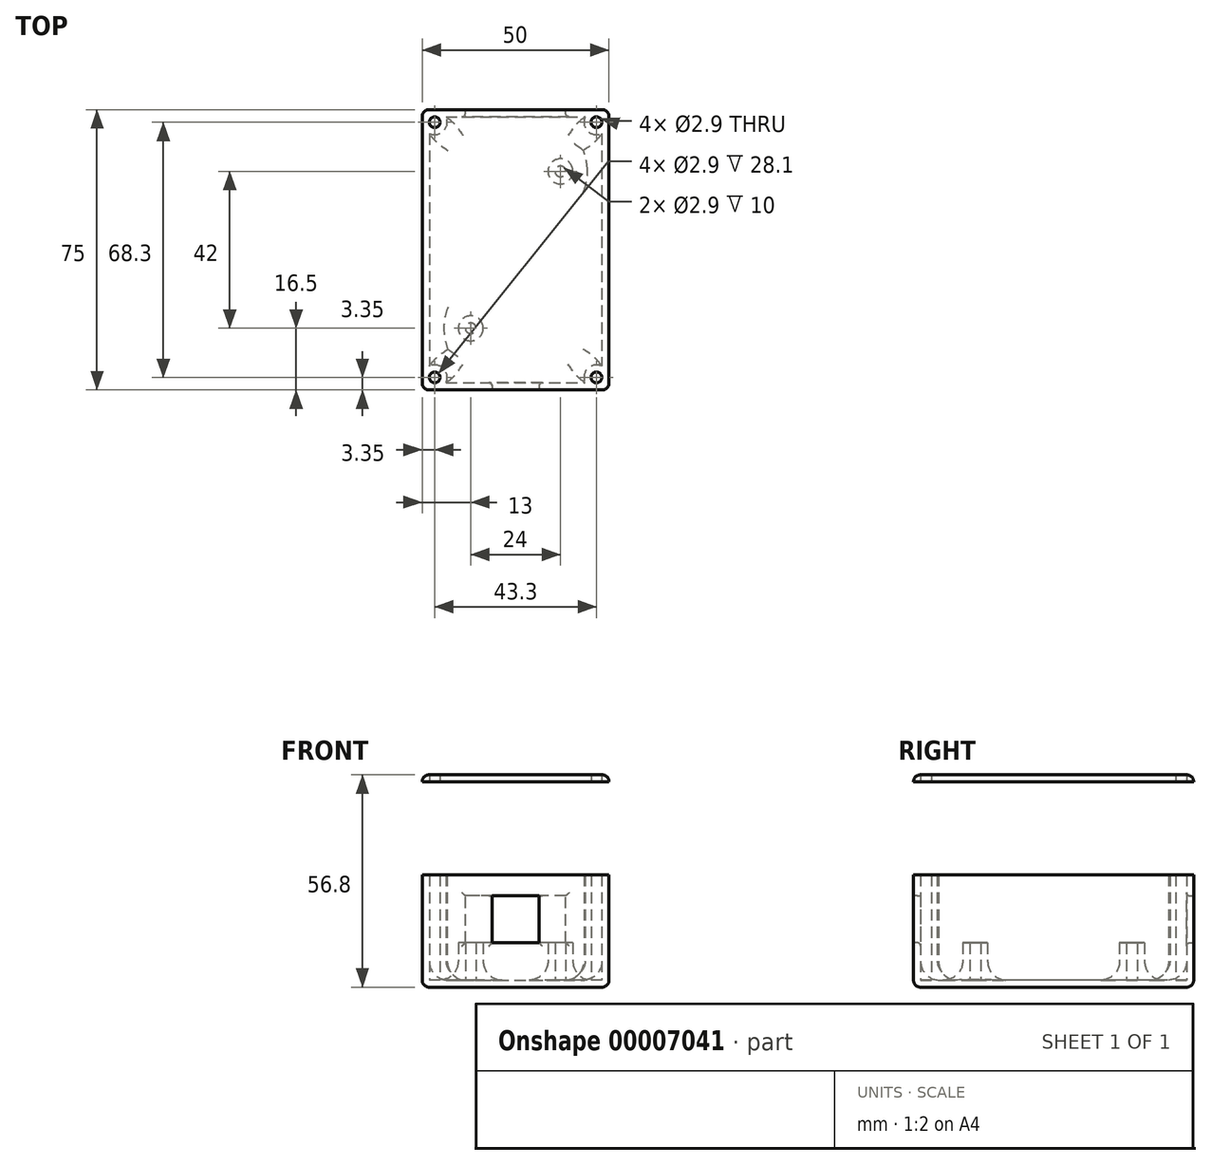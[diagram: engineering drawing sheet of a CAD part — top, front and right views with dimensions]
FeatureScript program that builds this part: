
annotation { "Feature Type Name" : "Feature", "Feature Type Description" : "" }
export const myFeature = defineFeature(function(context is Context, id is Id, definition is map)
    precondition{}
    {
        {
            var Q0;
            Q0=qCreatedBy(makeId("Top.planeOp"),FACE);
            var sketch = newSketch(context, id + "F0", { "sketchPlane" : qUnion([Q0])});
            skLineSegment(sketch, "E0.bottom", {"start": v(-25, 37.5) * mm, "end": v(25, 37.5) * mm});
            skLineSegment(sketch, "E0.top", {"start": v(-25, -37.5) * mm, "end": v(25, -37.5) * mm});
            skLineSegment(sketch, "E0.left", {"start": v(-25, 37.5) * mm, "end": v(-25, -37.5) * mm});
            skLineSegment(sketch, "E0.right", {"start": v(25, 37.5) * mm, "end": v(25, -37.5) * mm});
            skSolve(sketch);
        }
        {
            var Q0;
            Q0 = qSketchRegion(id + "F0", true);
            extrude(context, id + "F1", {"entities" : qUnion([Q0]), "depth" : 30 * mm});
        }
        {
            var Q0;
            Q0=makeQuery(id+"F1.opExtrude","CAP_FACE",FACE,{"disambiguationData":[OSD([sQuery(id+"F0.wireOp",EDGE,"E0.bottom"),sQuery(id+"F0.wireOp",EDGE,"E0.top"),sQuery(id+"F0.wireOp",EDGE,"E0.left"),sQuery(id+"F0.wireOp",EDGE,"E0.right")])],"isStart":false});
            shell(context, id + "F2", {"entities" : qUnion([Q0]), "thickness" : 1.9 * mm});
        }
        {
            var Q0;
            Q0=makeQuery(id+"F2.opShell","OFFSET_FACE",FACE,{"disambiguationData":[OSD([sQuery(id+"F0.wireOp",EDGE,"E0.bottom"),sQuery(id+"F0.wireOp",EDGE,"E0.top"),sQuery(id+"F0.wireOp",EDGE,"E0.left"),sQuery(id+"F0.wireOp",EDGE,"E0.right")])]});
            var sketch = newSketch(context, id + "F3", { "sketchPlane" : qUnion([Q0])});
            skCircle(sketch, "E1", {"center": v(12, 21) * mm, "radius": 1.45 * mm});
            skCircle(sketch, "E2", {"center": v(12, 21) * mm, "radius": 3.35 * mm});
            skCircle(sketch, "E3", {"center": v(-12, -21) * mm, "radius": 1.45 * mm});
            skCircle(sketch, "E4", {"center": v(-12, -21) * mm, "radius": 3.35 * mm});
            skLineSegment(sketch, "E5.bottom", {"start": v(-12, 21) * mm, "end": v(12, 21) * mm, "construction": true});
            skLineSegment(sketch, "E5.top", {"start": v(-12, -21) * mm, "end": v(12, -21) * mm, "construction": true});
            skLineSegment(sketch, "E5.left", {"start": v(-12, 21) * mm, "end": v(-12, -21) * mm, "construction": true});
            skLineSegment(sketch, "E5.right", {"start": v(12, 21) * mm, "end": v(12, -21) * mm, "construction": true});
            skCircle(sketch, "E6", {"center": v(-21.65, 34.15) * mm, "radius": 1.45 * mm});
            skCircle(sketch, "E7", {"center": v(-21.65, 34.15) * mm, "radius": 3.35 * mm});
            skCircle(sketch, "E8", {"center": v(21.65, 34.15) * mm, "radius": 1.45 * mm});
            skCircle(sketch, "E9", {"center": v(21.65, 34.15) * mm, "radius": 3.35 * mm});
            skCircle(sketch, "E10", {"center": v(21.65, -34.15) * mm, "radius": 1.45 * mm});
            skCircle(sketch, "E11", {"center": v(21.65, -34.15) * mm, "radius": 3.35 * mm});
            skCircle(sketch, "E12", {"center": v(-21.65, -34.15) * mm, "radius": 1.45 * mm});
            skCircle(sketch, "E13", {"center": v(-21.65, -34.15) * mm, "radius": 3.35 * mm});
            skLineSegment(sketch, "E14", {"start": v(12, 21) * mm, "end": v(12, 22.45) * mm, "construction": true});
            skLineSegment(sketch, "E15", {"start": v(12, 22.45) * mm, "end": v(12, 24.35) * mm, "construction": true});
            skSolve(sketch);
        }
        {
            var Q0;
            Q0=makeQuery(id+"F3.imprint","IMPRINT",FACE,{"disambiguationData":[TD([[makeQuery(id+"F3.imprint","IMPRINT",EDGE,{"derivedFrom":sQuery(id+"F3.wireOp",EDGE,"E1")}),-1.0]])]});
            var Q1;
            Q1=makeQuery(id+"F3.imprint","IMPRINT",FACE,{"disambiguationData":[TD([[makeQuery(id+"F3.imprint","IMPRINT",EDGE,{"derivedFrom":sQuery(id+"F3.wireOp",EDGE,"E3")}),-1.0]])]});
            extrude(context, id + "F4", {"entities" : qUnion([Q0, Q1]), "operationType" : NewBodyOperationType.ADD, "depth" : 10 * mm});
        }
        {
            var Q0;
            Q0=makeQuery(id+"F1.opExtrude","SWEPT_FACE",FACE,{"disambiguationData":[OSD([sQuery(id+"F0.wireOp",EDGE,"E0.bottom")])]});
            var sketch = newSketch(context, id + "F5", { "sketchPlane" : qUnion([Q0])});
            skLineSegment(sketch, "E16.0", {"start": v(10.55, 11.9) * mm, "end": v(13.45, 11.9) * mm});
            skLineSegment(sketch, "E17.0", {"start": v(-13.45, 11.9) * mm, "end": v(-10.55, 11.9) * mm});
            skLineSegment(sketch, "E18.bottom", {"start": v(-13.45, 11.9) * mm, "end": v(13.45, 11.9) * mm});
            skLineSegment(sketch, "E18.top", {"start": v(-13.45, 24.4) * mm, "end": v(13.45, 24.4) * mm});
            skLineSegment(sketch, "E18.left", {"start": v(-13.45, 11.9) * mm, "end": v(-13.45, 24.4) * mm});
            skLineSegment(sketch, "E18.right", {"start": v(13.45, 11.9) * mm, "end": v(13.45, 24.4) * mm});
            skSolve(sketch);
        }
        {
            var Q0;
            Q0 = qSketchRegion(id + "F5", true);
            var Q1;
            Q1=makeQuery(id+"F2.opShell","OFFSET_FACE",FACE,{"disambiguationData":[OSD([sQuery(id+"F0.wireOp",EDGE,"E0.top")])]});
            extrude(context, id + "F6", {"entities" : qUnion([Q0]), "operationType" : NewBodyOperationType.REMOVE, "endBound" : BoundingType.UP_TO_SURFACE, "oppositeDirection" : true, "endBoundEntityFace" : qUnion([Q1]), "depth" : 25 * mm});
        }
        {
            var Q0;
            Q0=makeQuery(id+"F1.opExtrude","SWEPT_FACE",FACE,{"disambiguationData":[OSD([sQuery(id+"F0.wireOp",EDGE,"E0.top")])]});
            var sketch = newSketch(context, id + "F7", { "sketchPlane" : qUnion([Q0])});
            skLineSegment(sketch, "E19.0", {"start": v(-13.45, 11.9) * mm, "end": v(-10.55, 11.9) * mm});
            skLineSegment(sketch, "E20.0", {"start": v(10.55, 11.9) * mm, "end": v(13.45, 11.9) * mm});
            skLineSegment(sketch, "E21.bottom", {"start": v(-6.25, 11.9) * mm, "end": v(6.25, 11.9) * mm});
            skLineSegment(sketch, "E21.top", {"start": v(-6.25, 24.4) * mm, "end": v(6.25, 24.4) * mm});
            skLineSegment(sketch, "E21.left", {"start": v(-6.25, 11.9) * mm, "end": v(-6.25, 24.4) * mm});
            skLineSegment(sketch, "E21.right", {"start": v(6.25, 11.9) * mm, "end": v(6.25, 24.4) * mm});
            skLineSegment(sketch, "E22.0", {"start": v(13.45, 24.4) * mm, "end": v(-13.45, 24.4) * mm});
            skSolve(sketch);
        }
        {
            var Q0;
            Q0=makeQuery(id+"F7.imprint","IMPRINT",FACE,{"disambiguationData":[TD([[makeQuery(id+"F7.imprint","IMPRINT",EDGE,{"derivedFrom":sQuery(id+"F7.wireOp",EDGE,"E21.bottom")}),1.0]])]});
            var Q1;
            Q1=makeQuery(id+"F2.opShell","OFFSET_FACE",FACE,{"disambiguationData":[OSD([sQuery(id+"F0.wireOp",EDGE,"E0.bottom")])]});
            extrude(context, id + "F8", {"entities" : qUnion([Q0]), "operationType" : NewBodyOperationType.REMOVE, "endBound" : BoundingType.UP_TO_SURFACE, "oppositeDirection" : true, "endBoundEntityFace" : qUnion([Q1]), "depth" : 25 * mm});
        }
        {
            var Q0;
            {var subQ2=sQuery(id+"F3.wireOp",EDGE,"E6");var subQ6=sQuery(id+"F0.wireOp",EDGE,"E0.bottom");var subQ7=makeQuery(id+"F2.opShell","OFFSET_EDGE",EDGE,{"disambiguationData":[OSD([subQ6]),TDD([makeQuery(id+"F1.opExtrude","CAP_EDGE",EDGE,{"disambiguationData":[OSD([subQ6])],"isStart":true})])]});var subQ8=makeQuery(id+"F3.imprint","INTERSECT",VERTEX,{"derivedFrom":[subQ7,subQ2]});Q0=makeQuery(id+"F3.imprint","IMPRINT",FACE,{"disambiguationData":[TD([[makeQuery(id+"F3.imprint","IMPRINT",EDGE,{"disambiguationData":[TD([[subQ8,1.0]])],"derivedFrom":subQ2}),-1.0]])]});}
            var Q1;
            {var subQ2=sQuery(id+"F3.wireOp",EDGE,"E8");var subQ6=sQuery(id+"F0.wireOp",EDGE,"E0.bottom");var subQ7=makeQuery(id+"F2.opShell","OFFSET_EDGE",EDGE,{"disambiguationData":[OSD([subQ6]),TDD([makeQuery(id+"F1.opExtrude","CAP_EDGE",EDGE,{"disambiguationData":[OSD([subQ6])],"isStart":true})])]});var subQ8=makeQuery(id+"F3.imprint","INTERSECT",VERTEX,{"derivedFrom":[subQ7,subQ2]});Q1=makeQuery(id+"F3.imprint","IMPRINT",FACE,{"disambiguationData":[TD([[makeQuery(id+"F3.imprint","IMPRINT",EDGE,{"disambiguationData":[TD([[subQ8,-1.0]])],"derivedFrom":subQ2}),-1.0]])]});}
            var Q2;
            {var subQ2=sQuery(id+"F3.wireOp",EDGE,"E8");var subQ4=sQuery(id+"F0.wireOp",EDGE,"E0.bottom");var subQ5=makeQuery(id+"F2.opShell","OFFSET_EDGE",EDGE,{"disambiguationData":[OSD([subQ4]),TDD([makeQuery(id+"F1.opExtrude","CAP_EDGE",EDGE,{"disambiguationData":[OSD([subQ4])],"isStart":true})])]});var subQ7=makeQuery(id+"F3.imprint","INTERSECT",VERTEX,{"derivedFrom":[subQ5,subQ2]});Q2=makeQuery(id+"F3.imprint","IMPRINT",FACE,{"disambiguationData":[TD([[makeQuery(id+"F3.imprint","IMPRINT",EDGE,{"disambiguationData":[TD([[subQ7,1.0]])],"derivedFrom":subQ2}),-1.0]])]});}
            var Q3;
            {var subQ2=sQuery(id+"F3.wireOp",EDGE,"E10");var subQ6=sQuery(id+"F0.wireOp",EDGE,"E0.top");var subQ7=makeQuery(id+"F2.opShell","OFFSET_EDGE",EDGE,{"disambiguationData":[OSD([subQ6]),TDD([makeQuery(id+"F1.opExtrude","CAP_EDGE",EDGE,{"disambiguationData":[OSD([subQ6])],"isStart":true})])]});var subQ8=makeQuery(id+"F3.imprint","INTERSECT",VERTEX,{"derivedFrom":[subQ7,subQ2]});Q3=makeQuery(id+"F3.imprint","IMPRINT",FACE,{"disambiguationData":[TD([[makeQuery(id+"F3.imprint","IMPRINT",EDGE,{"disambiguationData":[TD([[subQ8,1.0]])],"derivedFrom":subQ2}),-1.0]])]});}
            var Q4;
            {var subQ2=sQuery(id+"F3.wireOp",EDGE,"E10");var subQ4=sQuery(id+"F0.wireOp",EDGE,"E0.top");var subQ5=makeQuery(id+"F2.opShell","OFFSET_EDGE",EDGE,{"disambiguationData":[OSD([subQ4]),TDD([makeQuery(id+"F1.opExtrude","CAP_EDGE",EDGE,{"disambiguationData":[OSD([subQ4])],"isStart":true})])]});var subQ7=makeQuery(id+"F3.imprint","INTERSECT",VERTEX,{"derivedFrom":[subQ5,subQ2]});Q4=makeQuery(id+"F3.imprint","IMPRINT",FACE,{"disambiguationData":[TD([[makeQuery(id+"F3.imprint","IMPRINT",EDGE,{"disambiguationData":[TD([[subQ7,-1.0]])],"derivedFrom":subQ2}),-1.0]])]});}
            var Q5;
            {var subQ2=sQuery(id+"F3.wireOp",EDGE,"E12");var subQ4=sQuery(id+"F0.wireOp",EDGE,"E0.top");var subQ5=makeQuery(id+"F2.opShell","OFFSET_EDGE",EDGE,{"disambiguationData":[OSD([subQ4]),TDD([makeQuery(id+"F1.opExtrude","CAP_EDGE",EDGE,{"disambiguationData":[OSD([subQ4])],"isStart":true})])]});var subQ7=makeQuery(id+"F3.imprint","INTERSECT",VERTEX,{"derivedFrom":[subQ5,subQ2]});Q5=makeQuery(id+"F3.imprint","IMPRINT",FACE,{"disambiguationData":[TD([[makeQuery(id+"F3.imprint","IMPRINT",EDGE,{"disambiguationData":[TD([[subQ7,1.0]])],"derivedFrom":subQ2}),-1.0]])]});}
            var Q6;
            {var subQ2=sQuery(id+"F3.wireOp",EDGE,"E12");var subQ6=sQuery(id+"F0.wireOp",EDGE,"E0.top");var subQ7=makeQuery(id+"F2.opShell","OFFSET_EDGE",EDGE,{"disambiguationData":[OSD([subQ6]),TDD([makeQuery(id+"F1.opExtrude","CAP_EDGE",EDGE,{"disambiguationData":[OSD([subQ6])],"isStart":true})])]});var subQ9=makeQuery(id+"F3.imprint","INTERSECT",VERTEX,{"derivedFrom":[subQ7,subQ2]});Q6=makeQuery(id+"F3.imprint","IMPRINT",FACE,{"disambiguationData":[TD([[makeQuery(id+"F3.imprint","IMPRINT",EDGE,{"disambiguationData":[TD([[subQ9,-1.0]])],"derivedFrom":subQ2}),-1.0]])]});}
            var Q7;
            {var subQ2=sQuery(id+"F3.wireOp",EDGE,"E6");var subQ4=sQuery(id+"F0.wireOp",EDGE,"E0.bottom");var subQ5=makeQuery(id+"F2.opShell","OFFSET_EDGE",EDGE,{"disambiguationData":[OSD([subQ4]),TDD([makeQuery(id+"F1.opExtrude","CAP_EDGE",EDGE,{"disambiguationData":[OSD([subQ4])],"isStart":true})])]});var subQ7=makeQuery(id+"F3.imprint","INTERSECT",VERTEX,{"derivedFrom":[subQ5,subQ2]});Q7=makeQuery(id+"F3.imprint","IMPRINT",FACE,{"disambiguationData":[TD([[makeQuery(id+"F3.imprint","IMPRINT",EDGE,{"disambiguationData":[TD([[subQ7,-1.0]])],"derivedFrom":subQ2}),-1.0]])]});}
            var Q8;
            Q8=makeQuery(id+"F1.opExtrude","CAP_FACE",FACE,{"disambiguationData":[OSD([sQuery(id+"F0.wireOp",EDGE,"E0.bottom"),sQuery(id+"F0.wireOp",EDGE,"E0.top"),sQuery(id+"F0.wireOp",EDGE,"E0.left"),sQuery(id+"F0.wireOp",EDGE,"E0.right")])],"isStart":false});
            extrude(context, id + "F9", {"entities" : qUnion([Q0, Q1, Q2, Q3, Q4, Q5, Q6, Q7]), "operationType" : NewBodyOperationType.ADD, "endBound" : BoundingType.UP_TO_SURFACE, "endBoundEntityFace" : qUnion([Q8]), "depth" : 25 * mm});
        }
        {
            var Q0;
            {var subQ0=sQuery(id+"F3.wireOp",EDGE,"E12");var subQ1=sQuery(id+"F0.wireOp",EDGE,"E0.left");var subQ2=sQuery(id+"F0.wireOp",EDGE,"E0.top");var subQ3=sQuery(id+"F0.wireOp",EDGE,"E0.right");var subQ4=sQuery(id+"F0.wireOp",EDGE,"E0.bottom");var subQ5=sQuery(id+"F3.wireOp",EDGE,"E10");var subQ6=sQuery(id+"F3.wireOp",EDGE,"E8");var subQ7=sQuery(id+"F3.wireOp",EDGE,"E6");Q0=makeQuery(id+"F9.boolean.opBoolean","MERGE",FACE,{"derivedFrom":[makeQuery(id+"F1.opExtrude","CAP_FACE",FACE,{"disambiguationData":[OSD([subQ4,subQ2,subQ1,subQ3])],"isStart":false}),makeQuery(id+"F9.opExtrude","CAP_FACE",FACE,{"disambiguationData":[OSD([subQ4,subQ2,subQ1,subQ3]),ownerDisambiguation([makeQuery(id+"F9.opExtrude","SWEPT_BODY",BODY,{"disambiguationData":[OSD([subQ4,subQ1,subQ7])]})])],"isStart":false}),makeQuery(id+"F9.opExtrude","CAP_FACE",FACE,{"disambiguationData":[OSD([subQ4,subQ2,subQ1,subQ3]),ownerDisambiguation([makeQuery(id+"F9.opExtrude","SWEPT_BODY",BODY,{"disambiguationData":[OSD([subQ4,subQ1,subQ7,sQuery(id+"F3.wireOp",EDGE,"E7")])]})])],"isStart":false}),makeQuery(id+"F9.opExtrude","CAP_FACE",FACE,{"disambiguationData":[OSD([subQ4,subQ2,subQ1,subQ3]),ownerDisambiguation([makeQuery(id+"F9.opExtrude","SWEPT_BODY",BODY,{"disambiguationData":[OSD([subQ4,subQ3,subQ6])]})])],"isStart":false}),makeQuery(id+"F9.opExtrude","CAP_FACE",FACE,{"disambiguationData":[OSD([subQ4,subQ2,subQ1,subQ3]),ownerDisambiguation([makeQuery(id+"F9.opExtrude","SWEPT_BODY",BODY,{"disambiguationData":[OSD([subQ4,subQ3,subQ6,sQuery(id+"F3.wireOp",EDGE,"E9")])]})])],"isStart":false}),makeQuery(id+"F9.opExtrude","CAP_FACE",FACE,{"disambiguationData":[OSD([subQ4,subQ2,subQ1,subQ3]),ownerDisambiguation([makeQuery(id+"F9.opExtrude","SWEPT_BODY",BODY,{"disambiguationData":[OSD([subQ2,subQ3,subQ5,sQuery(id+"F3.wireOp",EDGE,"E11")])]})])],"isStart":false}),makeQuery(id+"F9.opExtrude","CAP_FACE",FACE,{"disambiguationData":[OSD([subQ4,subQ2,subQ1,subQ3]),ownerDisambiguation([makeQuery(id+"F9.opExtrude","SWEPT_BODY",BODY,{"disambiguationData":[OSD([subQ2,subQ3,subQ5])]})])],"isStart":false}),makeQuery(id+"F9.opExtrude","CAP_FACE",FACE,{"disambiguationData":[OSD([subQ4,subQ2,subQ1,subQ3]),ownerDisambiguation([makeQuery(id+"F9.opExtrude","SWEPT_BODY",BODY,{"disambiguationData":[OSD([subQ2,subQ1,subQ0])]})])],"isStart":false}),makeQuery(id+"F9.opExtrude","CAP_FACE",FACE,{"disambiguationData":[OSD([subQ4,subQ2,subQ1,subQ3]),ownerDisambiguation([makeQuery(id+"F9.opExtrude","SWEPT_BODY",BODY,{"disambiguationData":[OSD([subQ2,subQ1,subQ0,sQuery(id+"F3.wireOp",EDGE,"E13")])]})])],"isStart":false})]});}
            cPlane(context, id + "F10", {"entities" : qUnion([Q0]), "cplaneType" : CPlaneType.OFFSET, "offset" : 25 * mm, "width" : 150 * mm, "height" : 150 * mm});
        }
        {
            var Q0;
            Q0=qCreatedBy(id+"F10.planeOp",FACE);
            var sketch = newSketch(context, id + "F11", { "sketchPlane" : qUnion([Q0])});
            skLineSegment(sketch, "E23.0", {"start": v(-25, 37.5) * mm, "end": v(25, 37.5) * mm});
            skLineSegment(sketch, "E24.0", {"start": v(-25, 37.5) * mm, "end": v(-25, -37.5) * mm});
            skLineSegment(sketch, "E25.0", {"start": v(25, 37.5) * mm, "end": v(25, -37.5) * mm});
            skLineSegment(sketch, "E26.0", {"start": v(-25, -37.5) * mm, "end": v(25, -37.5) * mm});
            skCircle(sketch, "E27.0", {"center": v(-21.65, 34.15) * mm, "radius": 1.45 * mm});
            skCircle(sketch, "E28.0", {"center": v(21.65, 34.15) * mm, "radius": 1.45 * mm});
            skCircle(sketch, "E29.0", {"center": v(21.65, -34.15) * mm, "radius": 1.45 * mm});
            skCircle(sketch, "E30.0", {"center": v(-21.65, -34.15) * mm, "radius": 1.45 * mm});
            skSolve(sketch);
        }
        {
            var Q0;
            Q0=makeQuery(id+"F11.imprint","IMPRINT",FACE,{"disambiguationData":[TD([[makeQuery(id+"F11.imprint","IMPRINT",EDGE,{"derivedFrom":sQuery(id+"F11.wireOp",EDGE,"E23.0")}),-1.0]])]});
            extrude(context, id + "F12", {"entities" : qUnion([Q0]), "depth" : 1.8 * mm});
        }
        {
            var Q0;
            Q0=makeQuery(id+"F12.opExtrude","CAP_EDGE",EDGE,{"disambiguationData":[OSD([sQuery(id+"F11.wireOp",EDGE,"E24.0")])],"isStart":false});
            var Q1;
            Q1=makeQuery(id+"F12.opExtrude","CAP_EDGE",EDGE,{"disambiguationData":[OSD([sQuery(id+"F11.wireOp",EDGE,"E23.0")])],"isStart":false});
            var Q2;
            Q2=makeQuery(id+"F12.opExtrude","SWEPT_EDGE",EDGE,{"disambiguationData":[OSD([sQuery(id+"F11.wireOp",EDGE,"E23.0"),sQuery(id+"F11.wireOp",EDGE,"E24.0")])]});
            var Q3;
            Q3=makeQuery(id+"F12.opExtrude","SWEPT_EDGE",EDGE,{"disambiguationData":[OSD([sQuery(id+"F11.wireOp",EDGE,"E23.0"),sQuery(id+"F11.wireOp",EDGE,"E25.0")])]});
            var Q4;
            Q4=makeQuery(id+"F12.opExtrude","CAP_EDGE",EDGE,{"disambiguationData":[OSD([sQuery(id+"F11.wireOp",EDGE,"E25.0")])],"isStart":false});
            var Q5;
            Q5=makeQuery(id+"F12.opExtrude","CAP_EDGE",EDGE,{"disambiguationData":[OSD([sQuery(id+"F11.wireOp",EDGE,"E26.0")])],"isStart":false});
            var Q6;
            Q6=makeQuery(id+"F12.opExtrude","SWEPT_EDGE",EDGE,{"disambiguationData":[OSD([sQuery(id+"F11.wireOp",EDGE,"E24.0"),sQuery(id+"F11.wireOp",EDGE,"E26.0")])]});
            var Q7;
            Q7=makeQuery(id+"F12.opExtrude","SWEPT_EDGE",EDGE,{"disambiguationData":[OSD([sQuery(id+"F11.wireOp",EDGE,"E25.0"),sQuery(id+"F11.wireOp",EDGE,"E26.0")])]});
            var Q8;
            Q8=makeQuery(id+"F1.opExtrude","SWEPT_EDGE",EDGE,{"disambiguationData":[OSD([sQuery(id+"F0.wireOp",EDGE,"E0.bottom"),sQuery(id+"F0.wireOp",EDGE,"E0.right")])]});
            var Q9;
            Q9=makeQuery(id+"F1.opExtrude","SWEPT_EDGE",EDGE,{"disambiguationData":[OSD([sQuery(id+"F0.wireOp",EDGE,"E0.top"),sQuery(id+"F0.wireOp",EDGE,"E0.right")])]});
            var Q10;
            Q10=makeQuery(id+"F1.opExtrude","SWEPT_EDGE",EDGE,{"disambiguationData":[OSD([sQuery(id+"F0.wireOp",EDGE,"E0.top"),sQuery(id+"F0.wireOp",EDGE,"E0.left")])]});
            var Q11;
            Q11=makeQuery(id+"F1.opExtrude","SWEPT_EDGE",EDGE,{"disambiguationData":[OSD([sQuery(id+"F0.wireOp",EDGE,"E0.bottom"),sQuery(id+"F0.wireOp",EDGE,"E0.left")])]});
            var Q12;
            Q12=makeQuery(id+"F1.opExtrude","CAP_FACE",FACE,{"disambiguationData":[OSD([sQuery(id+"F0.wireOp",EDGE,"E0.bottom"),sQuery(id+"F0.wireOp",EDGE,"E0.top"),sQuery(id+"F0.wireOp",EDGE,"E0.left"),sQuery(id+"F0.wireOp",EDGE,"E0.right")])],"isStart":true});
            fillet(context, id + "F13", {"entities" : qUnion([Q0, Q1, Q2, Q3, Q4, Q5, Q6, Q7, Q8, Q9, Q10, Q11, Q12]), "radius" : 1.8 * mm, "tangentPropagation" : true, "allowEdgeOverflow" : false});
        }
        {
            var Q0;
            {var subQ0=sQuery(id+"F0.wireOp",EDGE,"E0.right");var subQ2=sQuery(id+"F0.wireOp",EDGE,"E0.left");var subQ4=sQuery(id+"F0.wireOp",EDGE,"E0.top");var subQ6=sQuery(id+"F0.wireOp",EDGE,"E0.bottom");var subQ7=makeQuery(id+"F2.opShell","OFFSET_FACE",FACE,{"disambiguationData":[OSD([subQ6])]});Q0=makeQuery(id+"F9.boolean.opBoolean","SPLIT",FACE,{"disambiguationData":[TD([subQ7])],"derivedFrom":makeQuery(id+"F4.boolean.opBoolean","SPLIT",FACE,{"disambiguationData":[TD([subQ7])],"derivedFrom":makeQuery(id+"F2.opShell","OFFSET_FACE",FACE,{"disambiguationData":[OSD([subQ6,subQ4,subQ2,subQ0])]})})});}
            fillet(context, id + "F14", {"entities" : qUnion([Q0]), "radius" : 5 * mm, "tangentPropagation" : true, "allowEdgeOverflow" : false});
        }
        {
            var Q0;
            Q0=makeQuery(id+"F6.boolean.opBoolean","COPY",EDGE,{"derivedFrom":makeQuery(id+"F6.opExtrude","CAP_EDGE",EDGE,{"disambiguationData":[OSD([sQuery(id+"F5.wireOp",EDGE,"E18.bottom")])],"isStart":true})});
            var Q1;
            Q1=makeQuery(id+"F6.boolean.opBoolean","COPY",EDGE,{"derivedFrom":makeQuery(id+"F6.opExtrude","CAP_EDGE",EDGE,{"disambiguationData":[OSD([sQuery(id+"F5.wireOp",EDGE,"E18.right")])],"isStart":true})});
            var Q2;
            Q2=makeQuery(id+"F6.boolean.opBoolean","INTERSECT",EDGE,{"derivedFrom":[makeQuery(id+"F2.opShell","OFFSET_FACE",FACE,{"disambiguationData":[OSD([sQuery(id+"F0.wireOp",EDGE,"E0.bottom")])]}),makeQuery(id+"F6.opExtrude","SWEPT_FACE",FACE,{"disambiguationData":[OSD([sQuery(id+"F5.wireOp",EDGE,"E18.right")])]})]});
            var Q3;
            Q3=makeQuery(id+"F6.boolean.opBoolean","INTERSECT",EDGE,{"derivedFrom":[makeQuery(id+"F2.opShell","OFFSET_FACE",FACE,{"disambiguationData":[OSD([sQuery(id+"F0.wireOp",EDGE,"E0.bottom")])]}),makeQuery(id+"F6.opExtrude","SWEPT_FACE",FACE,{"disambiguationData":[OSD([sQuery(id+"F5.wireOp",EDGE,"E18.bottom")])]})]});
            var Q4;
            Q4=makeQuery(id+"F8.boolean.opBoolean","COPY",EDGE,{"derivedFrom":makeQuery(id+"F8.opExtrude","CAP_EDGE",EDGE,{"disambiguationData":[OSD([sQuery(id+"F7.wireOp",EDGE,"E22.0")])],"isStart":true})});
            var Q5;
            Q5=makeQuery(id+"F8.boolean.opBoolean","COPY",EDGE,{"derivedFrom":makeQuery(id+"F8.opExtrude","CAP_EDGE",EDGE,{"disambiguationData":[OSD([sQuery(id+"F7.wireOp",EDGE,"E21.left")])],"isStart":true})});
            var Q6;
            Q6=makeQuery(id+"F8.boolean.opBoolean","COPY",EDGE,{"derivedFrom":makeQuery(id+"F8.opExtrude","CAP_EDGE",EDGE,{"disambiguationData":[OSD([sQuery(id+"F7.wireOp",EDGE,"E21.bottom")])],"isStart":true})});
            var Q7;
            Q7=makeQuery(id+"F8.boolean.opBoolean","COPY",EDGE,{"derivedFrom":makeQuery(id+"F8.opExtrude","CAP_EDGE",EDGE,{"disambiguationData":[OSD([sQuery(id+"F7.wireOp",EDGE,"E21.right")])],"isStart":true})});
            var Q8;
            Q8=makeQuery(id+"F8.boolean.opBoolean","INTERSECT",EDGE,{"derivedFrom":[makeQuery(id+"F2.opShell","OFFSET_FACE",FACE,{"disambiguationData":[OSD([sQuery(id+"F0.wireOp",EDGE,"E0.top")])]}),makeQuery(id+"F8.opExtrude","SWEPT_FACE",FACE,{"disambiguationData":[OSD([sQuery(id+"F7.wireOp",EDGE,"E21.right")])]})]});
            var Q9;
            Q9=makeQuery(id+"F8.boolean.opBoolean","INTERSECT",EDGE,{"derivedFrom":[makeQuery(id+"F2.opShell","OFFSET_FACE",FACE,{"disambiguationData":[OSD([sQuery(id+"F0.wireOp",EDGE,"E0.top")])]}),makeQuery(id+"F8.opExtrude","SWEPT_FACE",FACE,{"disambiguationData":[OSD([sQuery(id+"F7.wireOp",EDGE,"E21.bottom")])]})]});
            var Q10;
            Q10=makeQuery(id+"F6.boolean.opBoolean","INTERSECT",EDGE,{"derivedFrom":[makeQuery(id+"F2.opShell","OFFSET_FACE",FACE,{"disambiguationData":[OSD([sQuery(id+"F0.wireOp",EDGE,"E0.bottom")])]}),makeQuery(id+"F6.opExtrude","SWEPT_FACE",FACE,{"disambiguationData":[OSD([sQuery(id+"F5.wireOp",EDGE,"E18.top")])]})]});
            var Q11;
            Q11=makeQuery(id+"F6.boolean.opBoolean","INTERSECT",EDGE,{"derivedFrom":[makeQuery(id+"F2.opShell","OFFSET_FACE",FACE,{"disambiguationData":[OSD([sQuery(id+"F0.wireOp",EDGE,"E0.bottom")])]}),makeQuery(id+"F6.opExtrude","SWEPT_FACE",FACE,{"disambiguationData":[OSD([sQuery(id+"F5.wireOp",EDGE,"E18.left")])]})]});
            var Q12;
            Q12=makeQuery(id+"F6.boolean.opBoolean","COPY",EDGE,{"derivedFrom":makeQuery(id+"F6.opExtrude","CAP_EDGE",EDGE,{"disambiguationData":[OSD([sQuery(id+"F5.wireOp",EDGE,"E18.top")])],"isStart":true})});
            var Q13;
            Q13=makeQuery(id+"F6.boolean.opBoolean","COPY",EDGE,{"derivedFrom":makeQuery(id+"F6.opExtrude","CAP_EDGE",EDGE,{"disambiguationData":[OSD([sQuery(id+"F5.wireOp",EDGE,"E18.left")])],"isStart":true})});
            var Q14;
            Q14=makeQuery(id+"F8.boolean.opBoolean","INTERSECT",EDGE,{"derivedFrom":[makeQuery(id+"F2.opShell","OFFSET_FACE",FACE,{"disambiguationData":[OSD([sQuery(id+"F0.wireOp",EDGE,"E0.top")])]}),makeQuery(id+"F8.opExtrude","SWEPT_FACE",FACE,{"disambiguationData":[OSD([sQuery(id+"F7.wireOp",EDGE,"E22.0")])]})]});
            var Q15;
            Q15=makeQuery(id+"F8.boolean.opBoolean","INTERSECT",EDGE,{"derivedFrom":[makeQuery(id+"F2.opShell","OFFSET_FACE",FACE,{"disambiguationData":[OSD([sQuery(id+"F0.wireOp",EDGE,"E0.top")])]}),makeQuery(id+"F8.opExtrude","SWEPT_FACE",FACE,{"disambiguationData":[OSD([sQuery(id+"F7.wireOp",EDGE,"E21.left")])]})]});
            fillet(context, id + "F15", {"entities" : qUnion([Q0, Q1, Q2, Q3, Q4, Q5, Q6, Q7, Q8, Q9, Q10, Q11, Q12, Q13, Q14, Q15]), "radius" : .9 * mm, "tangentPropagation" : true, "allowEdgeOverflow" : false});
        }
    });
